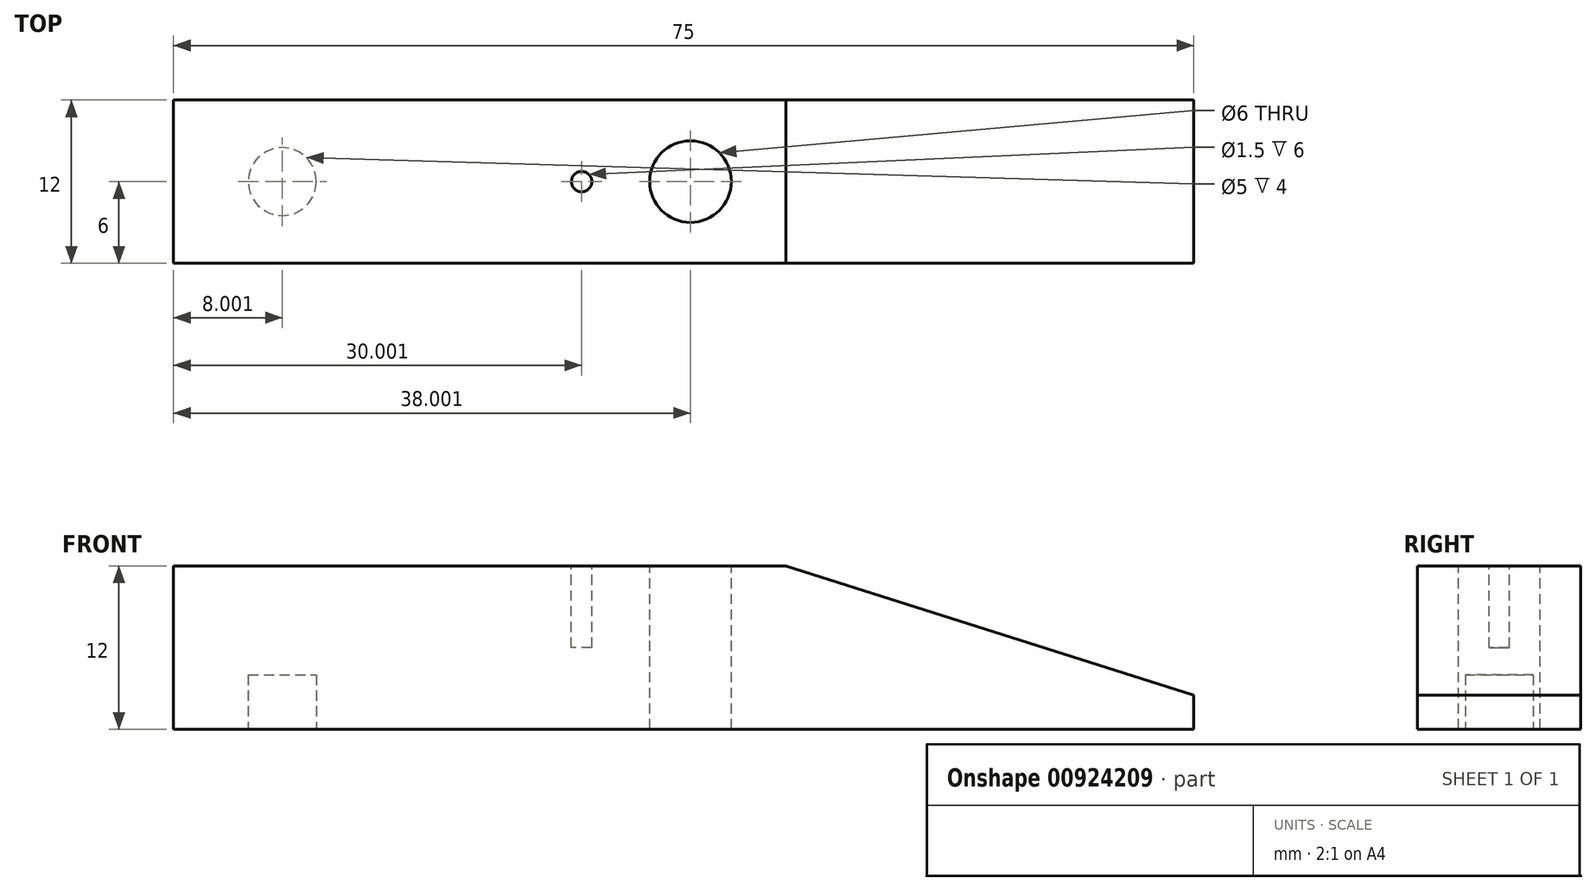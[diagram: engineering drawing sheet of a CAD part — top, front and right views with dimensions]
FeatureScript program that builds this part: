
annotation { "Feature Type Name" : "Feature", "Feature Type Description" : "" }
export const myFeature = defineFeature(function(context is Context, id is Id, definition is map)
    precondition{}
    {
        {
            var Q0;
            Q0=qCreatedBy(makeId("Front.planeOp"),FACE);
            var sketch = newSketch(context, id + "F0", { "sketchPlane" : qUnion([Q0])});
            skLineSegment(sketch, "E0", {"start": v(-38.3, 35.94) * mm, "end": v(6.7, 35.94) * mm});
            skLineSegment(sketch, "E1", {"start": v(6.7, 35.94) * mm, "end": v(36.7, 26.44) * mm});
            skLineSegment(sketch, "E2", {"start": v(36.7, 26.44) * mm, "end": v(36.7, 23.94) * mm});
            skLineSegment(sketch, "E3", {"start": v(36.7, 23.94) * mm, "end": v(-38.3, 23.94) * mm});
            skLineSegment(sketch, "E4", {"start": v(-38.3, 23.94) * mm, "end": v(-38.3, 35.94) * mm});
            skSolve(sketch);
        }
        {
            var Q0;
            Q0 = qSketchRegion(id + "F0", true);
            extrude(context, id + "F1", {"entities" : qUnion([Q0]), "depth" : 12 * mm, "offsetDistance" : 25 * mm});
        }
        {
            var Q0;
            Q0=makeQuery(id+"F1.opExtrude","SWEPT_FACE",FACE,{"disambiguationData":[OSD([sQuery(id+"F0.wireOp",EDGE,"E0")])]});
            var sketch = newSketch(context, id + "F2", { "sketchPlane" : qUnion([Q0])});
            skCircle(sketch, "E5", {"center": v(-0.3, -6) * mm, "radius": 3 * mm});
            skSolve(sketch);
        }
        {
            var Q0;
            Q0 = qSketchRegion(id + "F2", true);
            extrude(context, id + "F3", {"entities" : qUnion([Q0]), "operationType" : NewBodyOperationType.REMOVE, "oppositeDirection" : true, "depth" : 25 * mm, "offsetDistance" : 25 * mm});
        }
        {
            var Q0;
            Q0=makeQuery(id+"F1.opExtrude","SWEPT_FACE",FACE,{"disambiguationData":[OSD([sQuery(id+"F0.wireOp",EDGE,"E0")])]});
            var sketch = newSketch(context, id + "F4", { "sketchPlane" : qUnion([Q0])});
            skCircle(sketch, "E6", {"center": v(-8.3, -6) * mm, "radius": 0.75 * mm});
            skSolve(sketch);
        }
        {
            var Q0;
            Q0 = qSketchRegion(id + "F4", true);
            extrude(context, id + "F5", {"entities" : qUnion([Q0]), "operationType" : NewBodyOperationType.REMOVE, "oppositeDirection" : true, "depth" : 6 * mm, "offsetDistance" : 25 * mm});
        }
        {
            var Q0;
            Q0=makeQuery(id+"F1.opExtrude","SWEPT_FACE",FACE,{"disambiguationData":[OSD([sQuery(id+"F0.wireOp",EDGE,"E3")])]});
            var sketch = newSketch(context, id + "F6", { "sketchPlane" : qUnion([Q0])});
            skCircle(sketch, "E7", {"center": v(-30.3, 6) * mm, "radius": 2.5 * mm});
            skSolve(sketch);
        }
        {
            var Q0;
            Q0 = qSketchRegion(id + "F6", true);
            extrude(context, id + "F7", {"entities" : qUnion([Q0]), "operationType" : NewBodyOperationType.REMOVE, "oppositeDirection" : true, "depth" : 4 * mm, "offsetDistance" : 25 * mm});
        }
    });
